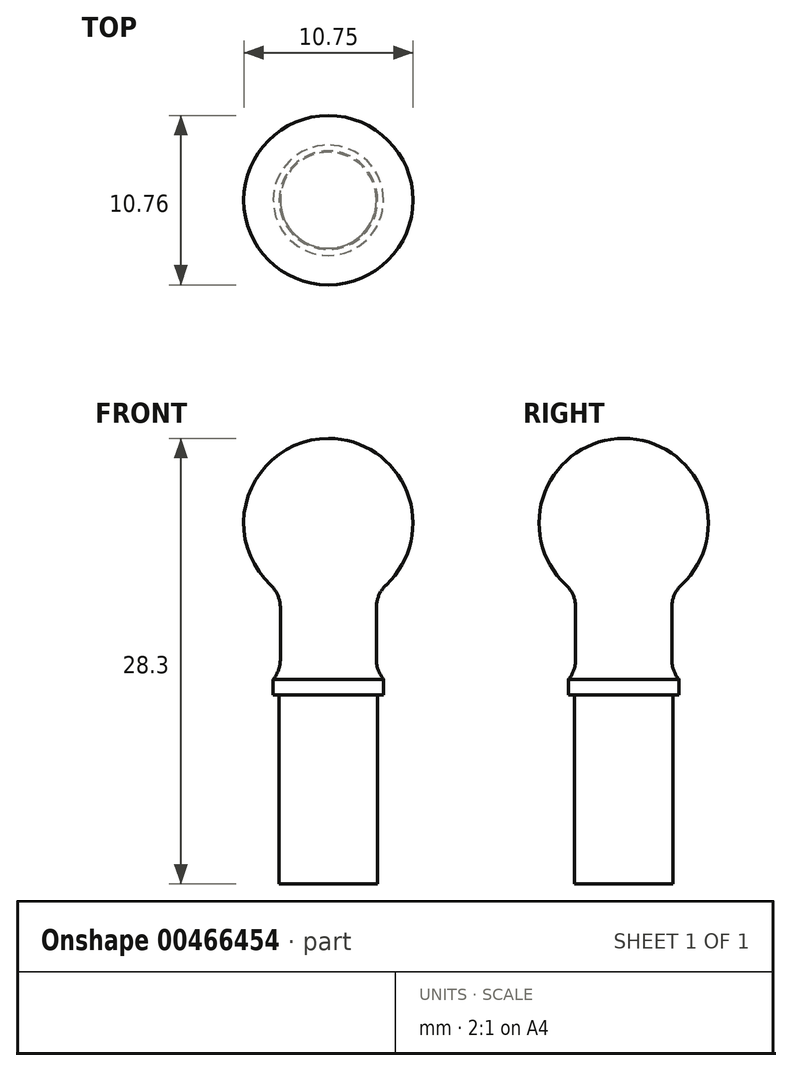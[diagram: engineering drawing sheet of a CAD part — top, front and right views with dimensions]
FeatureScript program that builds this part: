
annotation { "Feature Type Name" : "Feature", "Feature Type Description" : "" }
export const myFeature = defineFeature(function(context is Context, id is Id, definition is map)
    precondition{}
    {
        {
            var Q0;
            Q0=qCreatedBy(makeId("Front.planeOp"),FACE);
            var sketch = newSketch(context, id + "F0", { "sketchPlane" : qUnion([Q0])});
            skLineSegment(sketch, "E0", {"start": v(0, 39.63) * mm, "end": v(0, -23.74) * mm, "construction": true});
            skLineSegment(sketch, "E1", {"start": v(0, 0) * mm, "end": v(-3.12, 0) * mm});
            skLineSegment(sketch, "E2", {"start": v(-3.12, 0) * mm, "end": v(-3.12, 12) * mm});
            skLineSegment(sketch, "E3", {"start": v(-3.12, 12) * mm, "end": v(-3.5, 12) * mm});
            skLineSegment(sketch, "E4", {"start": v(-3.5, 12) * mm, "end": v(-3.5, 13) * mm});
            skLineSegment(sketch, "E5", {"start": v(-3.5, 13) * mm, "end": v(-3.05, 13) * mm});
            skLineSegment(sketch, "E6", {"start": v(-3.05, 13) * mm, "end": v(-3.05, 18.5) * mm});
            skArc(sketch, "E7", {"start": v(0, 28.3) * mm, "mid": v(-5.13, 24.52) * mm, "end": v(-3.05, 18.5) * mm});
            skLineSegment(sketch, "E8", {"start": v(0, 28.3) * mm, "end": v(-9.07, 28.3) * mm, "construction": true});
            skLineSegment(sketch, "E9", {"start": v(0, 28.3) * mm, "end": v(0, 0) * mm});
            skSolve(sketch);
        }
        {
            var Q0;
            Q0 = qSketchRegion(id + "F0", true);
            var Q1;
            Q1=sQuery(id+"F0.wireOp",EDGE,"E0");
            revolve(context, id + "F1", {"entities" : qUnion([Q0]), "axis" : qUnion([Q1]), "revolveType" : RevolveType.FULL});
        }
        {
            var Q0;
            Q0=makeQuery(id+"F1.opRevolve","SWEPT_EDGE",EDGE,{"disambiguationData":[OSD([sQuery(id+"F0.wireOp",EDGE,"E6"),sQuery(id+"F0.wireOp",EDGE,"E7")])]});
            var Q1;
            Q1=makeQuery(id+"F1.opRevolve","SWEPT_EDGE",EDGE,{"disambiguationData":[OSD([sQuery(id+"F0.wireOp",EDGE,"E5"),sQuery(id+"F0.wireOp",EDGE,"E6")])]});
            fillet(context, id + "F2", {"entities" : qUnion([Q0, Q1]), "radius" : 2 * mm, "tangentPropagation" : true, "allowEdgeOverflow" : false});
        }
    });
